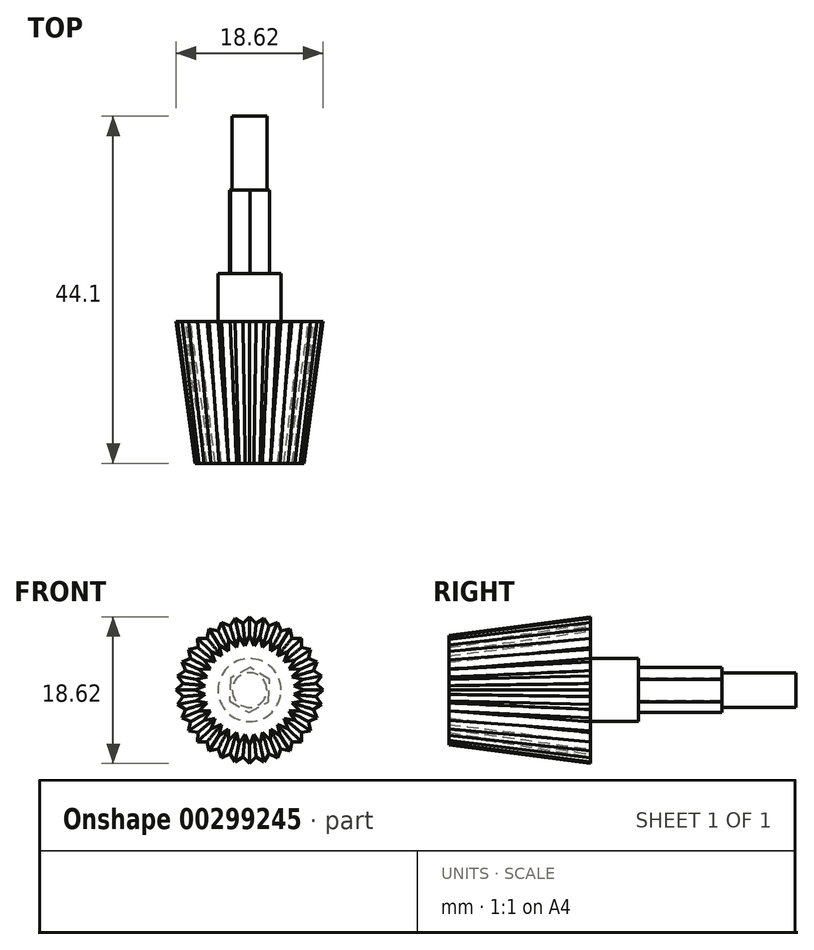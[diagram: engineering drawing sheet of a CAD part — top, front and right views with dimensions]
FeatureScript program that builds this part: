
annotation { "Feature Type Name" : "Feature", "Feature Type Description" : "" }
export const myFeature = defineFeature(function(context is Context, id is Id, definition is map)
    precondition{}
    {
        {
            var Q0;
            Q0=qCreatedBy(makeId("Front.planeOp"),FACE);
            var sketch = newSketch(context, id + "F0", { "sketchPlane" : qUnion([Q0])});
            skCircle(sketch, "E0", {"center": v(0, 0) * mm, "radius": 8.5 * mm});
            skSolve(sketch);
        }
        {
            var Q0;
            Q0=makeQuery(id+"F0.imprint","IMPRINT",FACE,{"disambiguationData":[TD([[makeQuery(id+"F0.imprint","IMPRINT",EDGE,{"derivedFrom":sQuery(id+"F0.wireOp",EDGE,"E0")}),1.0]])]});
            extrude(context, id + "F1", {"entities" : qUnion([Q0]), "depth" : 18 * mm, "hasDraft" : true, "draftAngle" : 9 * degree, "draftPullDirection" : true});
        }
        {
            var Q0;
            Q0=makeQuery(id+"F1.opExtrude","CAP_FACE",FACE,{"disambiguationData":[OSD([sQuery(id+"F0.wireOp",EDGE,"E0")])],"isStart":true});
            var sketch = newSketch(context, id + "F2", { "sketchPlane" : qUnion([Q0])});
            skCircle(sketch, "E1", {"center": v(0, 0) * mm, "radius": 4 * mm});
            skSolve(sketch);
        }
        {
            var Q0;
            Q0=makeQuery(id+"F2.imprint","IMPRINT",FACE,{"disambiguationData":[TD([[makeQuery(id+"F2.imprint","IMPRINT",EDGE,{"derivedFrom":sQuery(id+"F2.wireOp",EDGE,"E1")}),1.0]])]});
            extrude(context, id + "F3", {"entities" : qUnion([Q0]), "operationType" : NewBodyOperationType.ADD, "depth" : 6.1 * mm});
        }
        {
            var Q0;
            Q0=makeQuery(id+"F3.opExtrude","CAP_FACE",FACE,{"disambiguationData":[OSD([sQuery(id+"F2.wireOp",EDGE,"E1")])],"isStart":false});
            var sketch = newSketch(context, id + "F4", { "sketchPlane" : qUnion([Q0])});
            skCircle(sketch, "E2.cCircle", {"center": v(0, 0) * mm, "radius": 2.49 * mm, "construction": true});
            skLineSegment(sketch, "E2.0", {"start": v(-2.53, 1.36) * mm, "end": v(-0.09, 2.87) * mm});
            skLineSegment(sketch, "E2.1", {"start": v(-0.09, 2.87) * mm, "end": v(2.44, 1.51) * mm});
            skLineSegment(sketch, "E2.2", {"start": v(2.44, 1.51) * mm, "end": v(2.53, -1.36) * mm});
            skLineSegment(sketch, "E2.3", {"start": v(2.53, -1.36) * mm, "end": v(0.09, -2.87) * mm});
            skLineSegment(sketch, "E2.4", {"start": v(0.09, -2.87) * mm, "end": v(-2.44, -1.51) * mm});
            skLineSegment(sketch, "E2.5", {"start": v(-2.44, -1.51) * mm, "end": v(-2.53, 1.36) * mm});
            skPoint(sketch, "E2.0.midPoint", {"position": v(-1.3, 2.11) * mm});
            skSolve(sketch);
        }
        {
            var Q0;
            Q0=makeQuery(id+"F4.imprint","IMPRINT",FACE,{"disambiguationData":[TD([[makeQuery(id+"F4.imprint","IMPRINT",EDGE,{"derivedFrom":sQuery(id+"F4.wireOp",EDGE,"E2.0")}),-1.0]])]});
            extrude(context, id + "F5", {"entities" : qUnion([Q0]), "operationType" : NewBodyOperationType.ADD, "depth" : 10.6 * mm});
        }
        {
            var Q0;
            Q0=makeQuery(id+"F5.opExtrude","CAP_FACE",FACE,{"disambiguationData":[OSD([sQuery(id+"F4.wireOp",EDGE,"E2.0"),sQuery(id+"F4.wireOp",EDGE,"E2.1"),sQuery(id+"F4.wireOp",EDGE,"E2.2"),sQuery(id+"F4.wireOp",EDGE,"E2.3"),sQuery(id+"F4.wireOp",EDGE,"E2.4"),sQuery(id+"F4.wireOp",EDGE,"E2.5")])],"isStart":false});
            var sketch = newSketch(context, id + "F6", { "sketchPlane" : qUnion([Q0])});
            skCircle(sketch, "E3", {"center": v(0, 0) * mm, "radius": 2.2 * mm});
            skSolve(sketch);
        }
        {
            var Q0;
            Q0=makeQuery(id+"F6.imprint","IMPRINT",FACE,{"disambiguationData":[TD([[makeQuery(id+"F6.imprint","IMPRINT",EDGE,{"derivedFrom":sQuery(id+"F6.wireOp",EDGE,"E3")}),1.0]])]});
            extrude(context, id + "F7", {"entities" : qUnion([Q0]), "operationType" : NewBodyOperationType.ADD, "depth" : 9.4 * mm});
        }
        {
            var Q0;
            Q0=qCreatedBy(makeId("Front.planeOp"),FACE);
            var sketch = newSketch(context, id + "F8", { "sketchPlane" : qUnion([Q0])});
            skLineSegment(sketch, "E4", {"start": v(0, 9.3) * mm, "end": v(-0.84, 8.46) * mm});
            skLineSegment(sketch, "E5", {"start": v(-0.84, 8.46) * mm, "end": v(0.84, 8.46) * mm});
            skLineSegment(sketch, "E6", {"start": v(0.84, 8.46) * mm, "end": v(0, 9.3) * mm});
            skSolve(sketch);
        }
        {
            var Q0;
            Q0=makeQuery(id+"F1.opExtrude","CAP_FACE",FACE,{"disambiguationData":[OSD([sQuery(id+"F0.wireOp",EDGE,"E0")])],"isStart":false});
            var sketch = newSketch(context, id + "F9", { "sketchPlane" : qUnion([Q0])});
            skLineSegment(sketch, "E7", {"start": v(0, 6.94) * mm, "end": v(-0.56, 5.62) * mm});
            skLineSegment(sketch, "E8", {"start": v(-0.56, 5.62) * mm, "end": v(0.56, 5.62) * mm});
            skLineSegment(sketch, "E9", {"start": v(0.56, 5.62) * mm, "end": v(0, 6.94) * mm});
            skSolve(sketch);
        }
        {
            var Q1;
            {var subQ0=sQuery(id+"F9.wireOp",EDGE,"E7");Q1=makeQuery(id+"F9.imprint","IMPRINT",FACE,{"disambiguationData":[TD([[makeQuery(id+"F9.imprint","IMPRINT",EDGE,{"derivedFrom":subQ0}),1.0]])]});}
            var Q2;
            Q2=makeQuery(id+"F8.imprint","IMPRINT",FACE,{"disambiguationData":[TD([[makeQuery(id+"F8.imprint","IMPRINT",EDGE,{"derivedFrom":sQuery(id+"F8.wireOp",EDGE,"E4")}),1.0]])]});
            loft(context, id + "F10", {"sheetProfilesArray" : [{ "sheetProfileEntities" : qUnion([Q1]) }, { "sheetProfileEntities" : qUnion([Q2]) }]});
        }
        {
            var Q0;
            {var subQ0=sQuery(id+"F9.wireOp",EDGE,"E7");Q0=makeQuery(id+"F10.opLoft","SWEPT_BODY",BODY,{"disambiguationData":[OSD([makeQuery(id+"F8.imprint","IMPRINT",FACE,{"disambiguationData":[TD([[makeQuery(id+"F8.imprint","IMPRINT",EDGE,{"derivedFrom":sQuery(id+"F8.wireOp",EDGE,"E4")}),1.0]])]}),makeQuery(id+"F9.imprint","IMPRINT",FACE,{"disambiguationData":[TD([[makeQuery(id+"F9.imprint","IMPRINT",EDGE,{"derivedFrom":subQ0}),1.0]])]})])]});}
            var Q1;
            Q1=makeQuery(id+"F1.opExtrude","CAP_EDGE",EDGE,{"disambiguationData":[OSD([sQuery(id+"F0.wireOp",EDGE,"E0")])],"isStart":false});
            circularPattern(context, id + "F11", {"operationType" : NewBodyOperationType.ADD, "entities" : qUnion([Q0]), "axis" : qUnion([Q1]), "angle" : 360 * degree, "instanceCount" : 32, "equalSpace" : true});
        }
    });
